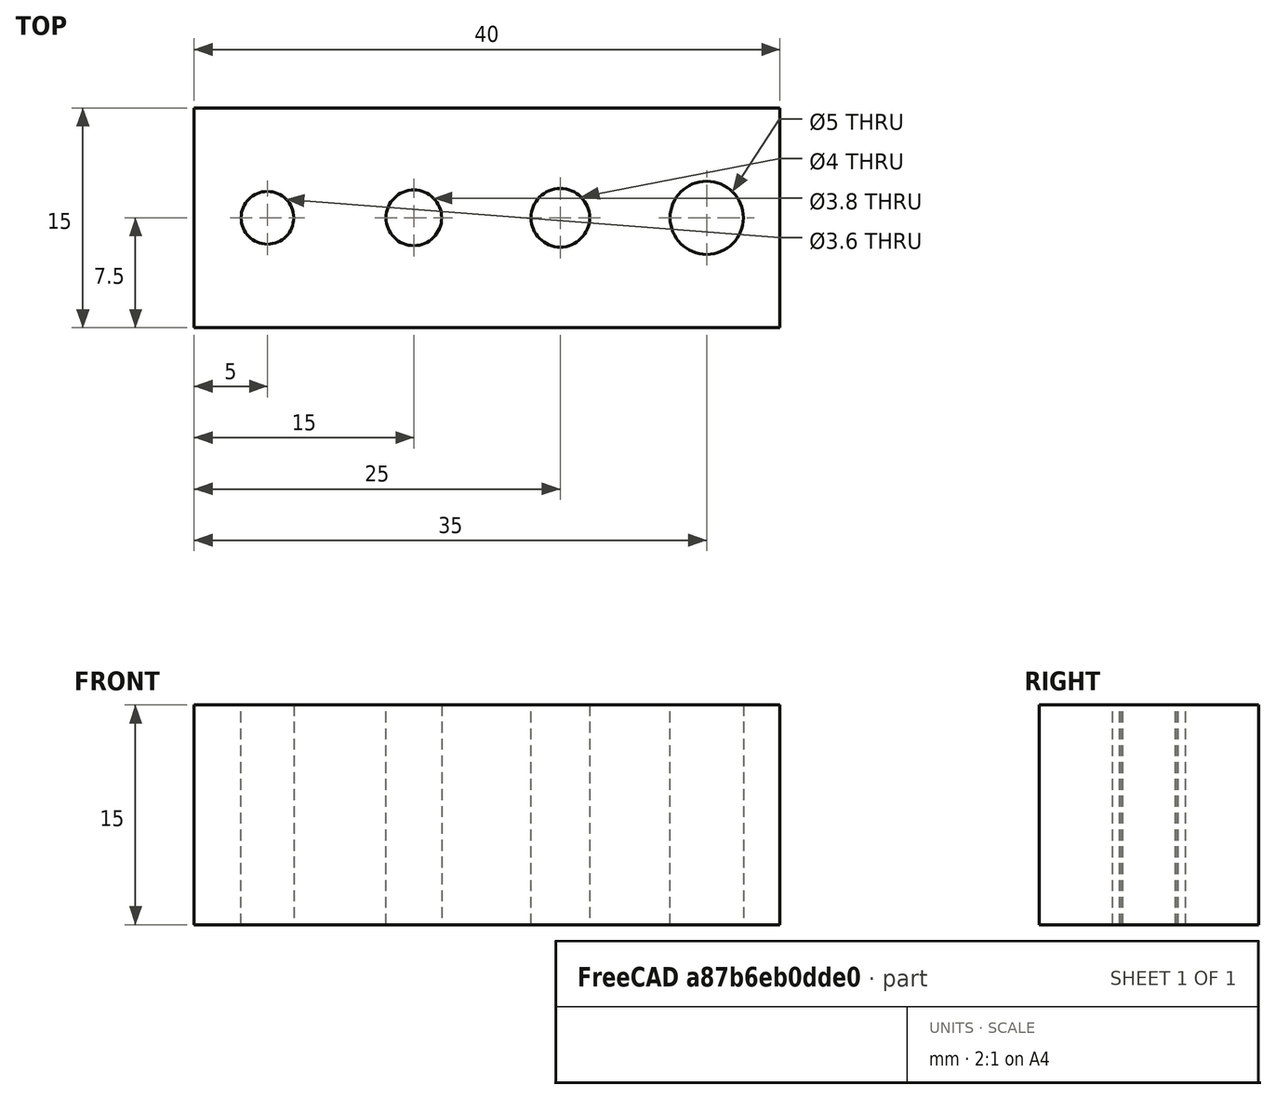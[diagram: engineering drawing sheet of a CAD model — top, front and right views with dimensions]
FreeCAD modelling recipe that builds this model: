
FCSTD DOCUMENT  (FreeCAD 0.19R)
Label: ScrewTest
License: All rights reserved
LicenseURL: http://en.wikipedia.org/wiki/All_rights_reserved
objects: Sketcher::SketchObject×2, PartDesign::Pad×1, PartDesign::Pocket×1, PartDesign::Body×1, Mesh::Feature×1
note: 7 computed .brp shape members not serialized (recipe doc carries the construction recipe); baked Part::Feature solids carry a one-line shape summary decoded from their .brp

FEATURE [Sketcher::SketchObject] Sketch
  FullyConstrained = true
  MapMode = 5
  Support = -> [XY_Plane]
  sketch-geometry (4):
    g0: LineSegment StartX=-20 StartY=7.5 StartZ=0 EndX=20 EndY=7.5 EndZ=0
    g1: LineSegment StartX=20 StartY=7.5 StartZ=0 EndX=20 EndY=-7.5 EndZ=0
    g2: LineSegment StartX=20 StartY=-7.5 StartZ=0 EndX=-20 EndY=-7.5 EndZ=0
    g3: LineSegment StartX=-20 StartY=-7.5 StartZ=0 EndX=-20 EndY=7.5 EndZ=0
  constraints (11):
    c: Coincident(g0,g1)
    c: Coincident(g1,g2)
    c: Coincident(g2,g3)
    c: Coincident(g3,g0)
    c: Horizontal(g0)
    c: Horizontal(g2)
    c: Vertical(g1)
    c: Vertical(g3)
    c: Symmetric(g1,g0,g-1)
    c: Distance(g0) = 40
    c: Distance(g1) = 15
FEATURE [PartDesign::Pad] Pad
  Direction = (1,1,1)
  Length = 15
  Length2 = 100
  Profile = -> Sketch
  Type = 0
FEATURE [Sketcher::SketchObject] Sketch001
  FullyConstrained = true
  MapMode = 5
  Placement = pos=(0,0,15) rot=(0,0,1;0rad)
  Support = -> [Pad]
  sketch-geometry (4):
    g0: Circle CenterX=-15 CenterY=0 CenterZ=0 NormalX=0 NormalY=0 NormalZ=1 AngleXU=0 Radius=1.8
    g1: Circle CenterX=-5 CenterY=0 CenterZ=0 NormalX=0 NormalY=0 NormalZ=1 AngleXU=0 Radius=1.9
    g2: Circle CenterX=5 CenterY=0 CenterZ=0 NormalX=0 NormalY=0 NormalZ=1 AngleXU=0 Radius=2
    g3: Circle CenterX=15 CenterY=0 CenterZ=0 NormalX=0 NormalY=0 NormalZ=1 AngleXU=0 Radius=2.5
  constraints (12):
    c: Diameter(g0) = 3.6
    c: Diameter(g1) = 3.8
    c: Diameter(g2) = 4
    c: Diameter(g3) = 5
    c: PointOnObject(g3,g-1)
    c: PointOnObject(g2,g-1)
    c: PointOnObject(g1,g-1)
    c: PointOnObject(g0,g-1)
    c: DistanceX(g0) = -15
    c: DistanceX(g3) = 15
    c: DistanceX(g2) = 5
    c: DistanceX(g1) = -5
FEATURE [PartDesign::Pocket] Pocket
  BaseFeature = -> Pad
  Length = 19
  Length2 = 100
  Profile = -> Sketch001
  Type = 0
FEATURE [PartDesign::Body] Body
  Group = -> [Sketch,Pad,Sketch001,Pocket]
  Origin = -> Origin
  Tip = -> Pocket
FEATURE [Mesh::Feature] Mesh  label="Pocket (Meshed)"
